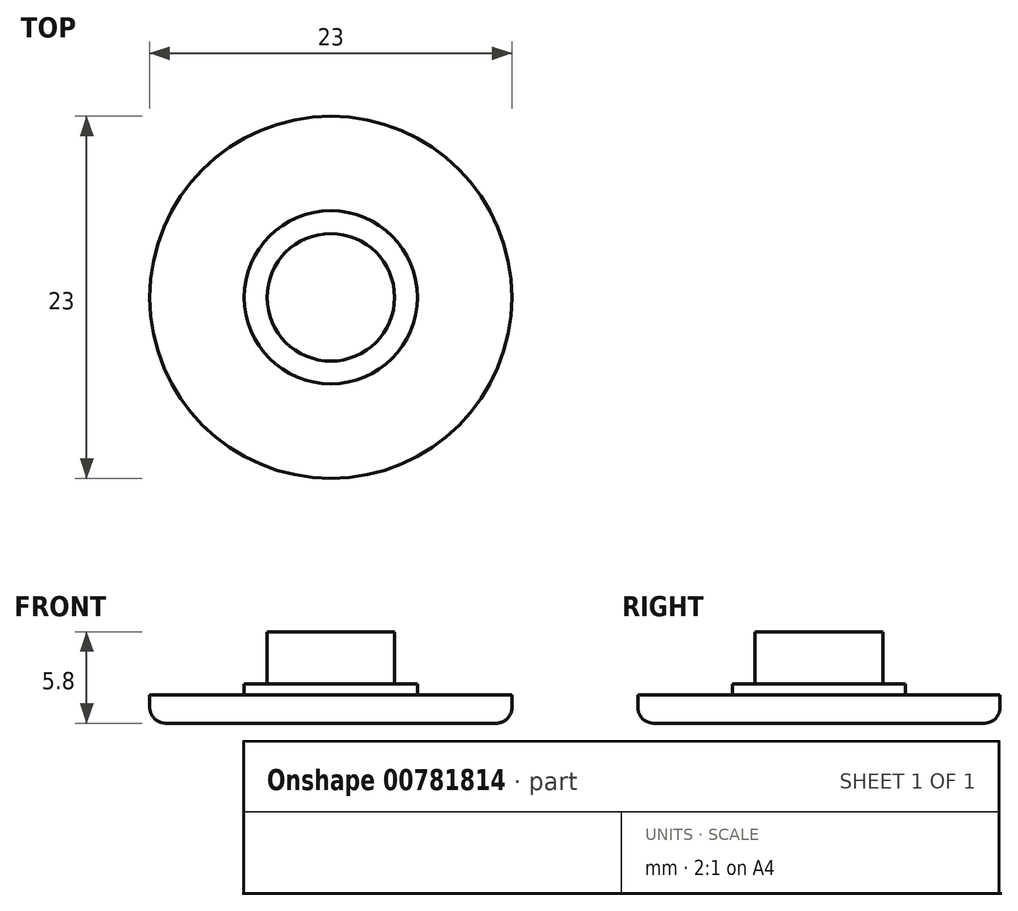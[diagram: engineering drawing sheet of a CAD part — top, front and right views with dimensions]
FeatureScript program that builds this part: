
annotation { "Feature Type Name" : "Feature", "Feature Type Description" : "" }
export const myFeature = defineFeature(function(context is Context, id is Id, definition is map)
    precondition{}
    {
        {
            var Q0;
            Q0=qCreatedBy(makeId("Top.planeOp"),FACE);
            var sketch = newSketch(context, id + "F0", { "sketchPlane" : qUnion([Q0])});
            skCircle(sketch, "E0", {"center": v(0, 0) * mm, "radius": 11.5 * mm});
            skCircle(sketch, "E1", {"center": v(0, 0) * mm, "radius": 5.5 * mm});
            skCircle(sketch, "E2", {"center": v(0, 0) * mm, "radius": 4.05 * mm});
            skSolve(sketch);
        }
        {
            var Q0;
            Q0=makeQuery(id+"F0.imprint","IMPRINT",FACE,{"disambiguationData":[TD([[makeQuery(id+"F0.imprint","IMPRINT",EDGE,{"derivedFrom":sQuery(id+"F0.wireOp",EDGE,"E0")}),1.0]])]});
            var Q1;
            Q1=makeQuery(id+"F0.imprint","IMPRINT",FACE,{"disambiguationData":[TD([[makeQuery(id+"F0.imprint","IMPRINT",EDGE,{"derivedFrom":sQuery(id+"F0.wireOp",EDGE,"E2")}),1.0]])]});
            var Q2;
            Q2=makeQuery(id+"F0.imprint","IMPRINT",FACE,{"disambiguationData":[TD([[makeQuery(id+"F0.imprint","IMPRINT",EDGE,{"derivedFrom":sQuery(id+"F0.wireOp",EDGE,"E1")}),1.0]])]});
            extrude(context, id + "F1", {"entities" : qUnion([Q0, Q1, Q2]), "oppositeDirection" : true, "depth" : 1.8 * mm, "offsetDistance" : 25 * mm});
        }
        {
            var Q0;
            Q0=makeQuery(id+"F0.imprint","IMPRINT",FACE,{"disambiguationData":[TD([[makeQuery(id+"F0.imprint","IMPRINT",EDGE,{"derivedFrom":sQuery(id+"F0.wireOp",EDGE,"E2")}),1.0]])]});
            extrude(context, id + "F2", {"entities" : qUnion([Q0]), "operationType" : NewBodyOperationType.ADD, "depth" : 4 * mm, "offsetDistance" : 25 * mm});
        }
        {
            var Q0;
            Q0=makeQuery(id+"F0.imprint","IMPRINT",FACE,{"disambiguationData":[TD([[makeQuery(id+"F0.imprint","IMPRINT",EDGE,{"derivedFrom":sQuery(id+"F0.wireOp",EDGE,"E1")}),1.0]])]});
            extrude(context, id + "F3", {"entities" : qUnion([Q0]), "operationType" : NewBodyOperationType.ADD, "depth" : 0.7 * mm, "offsetDistance" : 25 * mm});
        }
        {
            var Q0;
            Q0=makeQuery(id+"F1.opExtrude","CAP_EDGE",EDGE,{"disambiguationData":[OSD([sQuery(id+"F0.wireOp",EDGE,"E0")])],"isStart":false});
            fillet(context, id + "F4", {"entities" : qUnion([Q0]), "radius" : 1 * mm, "tangentPropagation" : true, "allowEdgeOverflow" : false});
        }
    });
